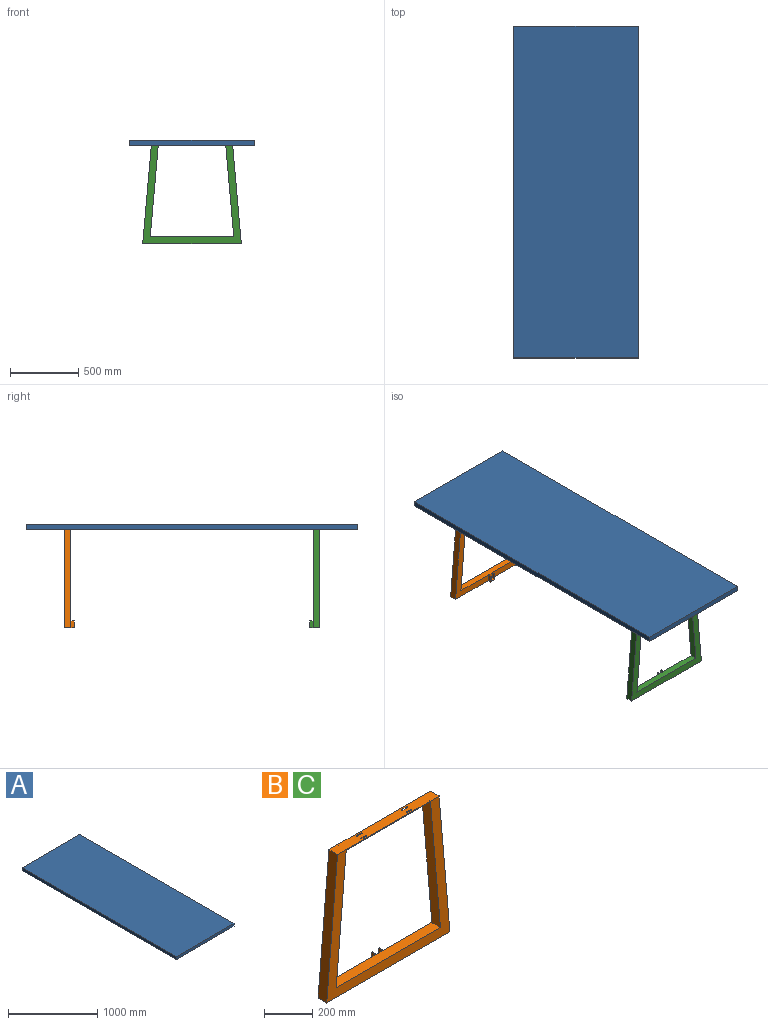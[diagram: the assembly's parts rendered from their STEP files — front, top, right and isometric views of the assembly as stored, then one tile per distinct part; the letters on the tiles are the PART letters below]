
ASSEMBLY  parts=3 mates=2
PART A: 6 faces, bbox 914.4x2438.4x38.1 mm
  f0: plane 2438.4x38.1mm, normal (1,0,0), area 92903mm2, adj f1,f3,f4,f5
  f1: plane 914.4x38.1mm, normal (0,1,0), area 34838.6mm2, adj f0,f2,f4,f5
  f2: plane 2438.4x38.1mm, normal (-1,0,0), area 92903mm2, adj f1,f3,f4,f5
  f3: plane 914.4x38.1mm, normal (0,-1,0), area 34838.6mm2, adj f0,f2,f4,f5
  f4: plane 2438.4x914.4mm, normal (0,0,1), area 2229673mm2, adj f0,f1,f2,f3
  f5: plane 2438.4x914.4mm, normal (0,0,-1), area 2229673mm2, adj f0,f1,f2,f3
PART B: 33 faces, bbox 723.9x76.2x723.9 mm
  f0: plane 723.9x723.9mm, normal (0,1,0), area 104511.8mm2, adj f1,f2,f3,f4,f5,f6,f7,f8
  f1: plane 495.8x50.8mm, normal (0,0,-1), area 24415mm2, adj f0,f3,f4,f9,f11,f12,f13,f14
  f2: plane 597.23x50.8mm, normal (0,0,1), area 29567.8mm2, adj f0,f5,f6,f9,f11,f12,f13,f14
  f3: plane 669.93x58.61mm, normal (1,0,-0.09), area 34162.2mm2, adj f0,f1,f8,f9
  f4: plane 669.93x58.61mm, normal (-1,0,-0.09), area 34162.2mm2, adj f0,f1,f8,f9
  f5: plane 723.9x63.33mm, normal (1,0,0.09), area 36914.6mm2, adj f0,f2,f7,f9
  f6: plane 723.9x63.33mm, normal (-1,0,0.09), area 36914.6mm2, adj f0,f2,f7,f9
  f7: plane 723.9x76.2mm, normal (0,0,-1), area 37903.1mm2, adj f0,f5,f6,f9,f29,f30,f32
  f8: plane 613.02x76.2mm, normal (0,0,1), area 31302.9mm2, adj f0,f3,f4,f9,f10,f28,f29,f30
  f9: plane 723.9x723.9mm, normal (0,-1,0), area 106769.8mm2, adj f1,f2,f3,f4,f5,f6,f7,f8
  f10: plane 47.63x38.1mm, normal (0,1,0), area 1814.5mm2, adj f8,f27,f28,f31
  f11: plane 25.31x3.18mm, normal (0,-1,0), area 80.4mm2, adj f1,f2,f12,f14
  f12: cylinder r=3.17mm len=6.35mm, axis (0,0,1), area 32.2mm2, adj f1,f2,f11,f13
  f13: plane 25.31x3.18mm, normal (0,1,0), area 80.4mm2, adj f1,f2,f12,f14
  f14: cylinder r=3.17mm len=6.35mm, axis (0,0,1), area 31.7mm2, adj f1,f2,f11,f13
  f15: cylinder r=3.17mm len=6.35mm, axis (0,0,1), area 32.2mm2, adj f1,f2,f16,f18
  f16: plane 25.31x3.18mm, normal (0,1,0), area 80.4mm2, adj f1,f2,f15,f17
  f17: cylinder r=3.17mm len=6.35mm, axis (0,0,1), area 31.7mm2, adj f1,f2,f16,f18
  f18: plane 25.31x3.18mm, normal (0,-1,0), area 80.4mm2, adj f1,f2,f15,f17
  f19: plane 25.31x3.18mm, normal (0,-1,0), area 80.4mm2, adj f1,f2,f20,f22
  f20: cylinder r=3.17mm len=6.35mm, axis (0,0,1), area 31.7mm2, adj f1,f2,f19,f21
  f21: plane 25.31x3.18mm, normal (0,1,0), area 80.4mm2, adj f1,f2,f20,f22
  f22: cylinder r=3.17mm len=6.35mm, axis (0,0,1), area 32.2mm2, adj f1,f2,f19,f21
  f23: cylinder r=3.17mm len=6.35mm, axis (0,0,1), area 32.2mm2, adj f1,f2,f24,f26
  f24: plane 25.31x3.18mm, normal (0,-1,0), area 80.4mm2, adj f1,f2,f23,f25
  f25: cylinder r=3.17mm len=6.35mm, axis (0,0,1), area 31.7mm2, adj f1,f2,f24,f26
  f26: plane 25.31x3.18mm, normal (0,1,0), area 80.4mm2, adj f1,f2,f23,f25
  f27: plane 38.1x25.4mm, normal (0,0,1), area 967.7mm2, adj f10,f28,f31,f32
  f28: plane 47.63x25.4mm, normal (-1,0,0), area 1209.7mm2, adj f8,f10,f27,f32
  f29: plane 50.8x25.4mm, normal (1,0,0), area 1290.3mm2, adj f0,f7,f8,f32
  f30: plane 50.8x25.4mm, normal (-1,0,0), area 1290.3mm2, adj f0,f7,f8,f32
  f31: plane 47.63x25.4mm, normal (1,0,0), area 1209.7mm2, adj f8,f10,f27,f32
  f32: plane 50.8x44.45mm, normal (0,1,0), area 443.5mm2, adj f7,f8,f27,f28,f29,f30,f31
PART C: same geometry as B
PLACE A t=(0,0,55.88)mm
PLACE B rot(axis=(0,0,1),180deg) t=(0,889.01,-306.07)mm
PLACE C t=(0,-889.01,-306.07)mm
MATE fastened C.f2 <-> A.f5  axis (0,0,1) through (0,-914.4,55.88)mm
MATE fastened B.f2 <-> A.f5  axis (0,0,1) through (0,914.4,55.88)mm
